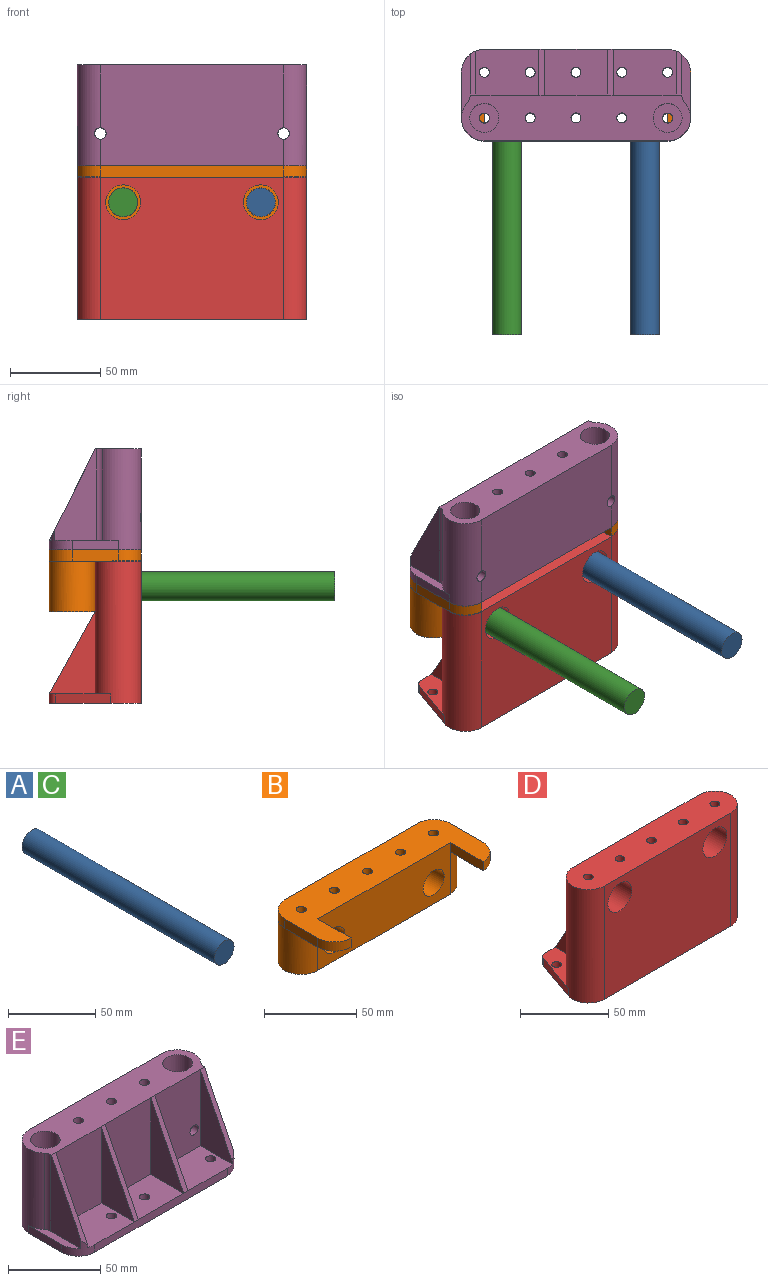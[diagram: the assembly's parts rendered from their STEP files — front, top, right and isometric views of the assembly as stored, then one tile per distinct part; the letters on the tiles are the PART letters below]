
ASSEMBLY  parts=5 mates=4
PART A: 3 faces, bbox 15.9x155.6x15.9 mm
  f0: cylinder r=7.94mm len=155.58mm, axis (0,1,0), area 7759mm2, adj f1,f2
  f1: plane 15.88x15.88mm, normal (0,-1,0), area 197.9mm2, adj f0
  f2: plane 15.88x15.88mm, normal (0,1,0), area 197.9mm2, adj f0
PART B: 29 faces, bbox 127x50.8x34.3 mm
  f0: plane 23.65x12.67mm, normal (0,0,-1), area 68.5mm2, adj f2,f7,f22
  f1: plane 25.39x6.35mm, normal (1,0,0), area 161mm2, adj f3,f5,f18,f19,f20,f21
  f2: plane 25.4x6.35mm, normal (-1,0,0), area 161.1mm2, adj f0,f8,f14,f15,f19,f22,f23
  f3: plane 24.52x12.7mm, normal (0,0,-1), area 68.9mm2, adj f1,f5,f21
  f4: plane 101.6x34.29mm, normal (0,-1,0), area 3075.2mm2, adj f5,f7,f9,f10,f12,f16,f17,f19
  f5: cylinder r=12.7mm len=34.29mm, axis (0,0,-1), area 1241.5mm2, adj f1,f3,f4,f6,f9,f19
  f6: plane 101.6x34.29mm, normal (0,1,0), area 3483.9mm2, adj f5,f7,f9,f14,f19
  f7: cylinder r=12.7mm len=27.94mm, axis (0,0,-1), area 1114.8mm2, adj f0,f4,f6,f8,f9
  f8: plane 13.58x12.7mm, normal (0,0,1), area 0.4mm2, adj f2,f7,f14
  f9: plane 127x25.4mm, normal (0,0,-1), area 2966.1mm2, adj f4,f5,f6,f7,f24,f25,f26,f27
  f10: cylinder r=8.06mm len=22.86mm, axis (0,-1,0), area 1158.3mm2, adj f4,f11
  f11: plane 16.13x16.13mm, normal (0,-1,0), area 204.3mm2, adj f10
  f12: cylinder r=8.06mm len=22.86mm, axis (0,-1,0), area 1158.3mm2, adj f4,f13
  f13: plane 16.13x16.13mm, normal (0,-1,0), area 204.3mm2, adj f12
  f14: cylinder r=12.7mm len=12.7mm, axis (0,0,-1), area 126.5mm2, adj f2,f6,f8,f19
  f15: cylinder r=12.7mm len=12.73mm, axis (0,0,-1), area 121.8mm2, adj f2,f16,f19,f23
  f16: plane 25.4x6.1mm, normal (1,0,0), area 154.8mm2, adj f4,f15,f19,f23
  f17: plane 25.4x6.1mm, normal (-1,0,0), area 154.8mm2, adj f4,f18,f19,f20
  f18: cylinder r=12.7mm len=12.73mm, axis (0,0,-1), area 121.8mm2, adj f1,f17,f19,f20
  f19: plane 126.97x50.8mm, normal (0,0,1), area 3610.5mm2, adj f1,f2,f4,f5,f6,f14,f15,f16
  f20: plane 25.4x12.73mm, normal (0,0,-1), area 253.7mm2, adj f1,f17,f18,f21
  f21: cylinder r=12.7mm len=12.67mm, axis (0,0,-1), area 4.8mm2, adj f1,f3,f4,f20
  f22: cylinder r=12.7mm len=12.67mm, axis (0,0,-1), area 4.8mm2, adj f0,f2,f4,f23
  f23: plane 25.4x12.73mm, normal (0,0,-1), area 253.7mm2, adj f2,f15,f16,f22
  f24: cylinder r=2.78mm len=34.29mm, axis (0,0,1), area 598.5mm2, adj f9,f19
  f25: cylinder r=2.78mm len=34.29mm, axis (0,0,1), area 598.5mm2, adj f9,f19
  f26: cylinder r=2.78mm len=34.29mm, axis (0,0,1), area 598.5mm2, adj f9,f19
  f27: cylinder r=2.78mm len=34.29mm, axis (0,0,1), area 598.5mm2, adj f9,f19
  f28: cylinder r=2.78mm len=34.29mm, axis (0,0,1), area 598.5mm2, adj f9,f19
PART C: same geometry as A
PART D: 40 faces, bbox 127x50.8x78.7 mm
  f0: plane 25.4x22.86mm, normal (0,0,1), area 556.4mm2, adj f5,f18,f24,f33,f35
  f1: plane 25.4x22.86mm, normal (0,0,1), area 556.4mm2, adj f5,f18,f23,f30,f32
  f2: plane 25.4x22.86mm, normal (0,0,1), area 556.4mm2, adj f5,f18,f22,f27,f29
  f3: plane 33.87x23.4mm, normal (0,0,1), area 392.5mm2, adj f5,f9,f18,f20,f21,f26,f38
  f4: plane 101.6x78.74mm, normal (0,-1,0), area 7414.6mm2, adj f6,f7,f8,f9,f10,f16
  f5: plane 101.6x73.66mm, normal (0,1,0), area 6434mm2, adj f0,f1,f2,f3,f6,f7,f8,f9
  f6: plane 127x25.4mm, normal (0,0,1), area 2966.1mm2, adj f4,f5,f9,f10,f11,f12,f13,f14
  f7: cylinder r=9.65mm len=25.4mm, axis (0,-1,0), area 1540.4mm2, adj f4,f5
  f8: cylinder r=9.65mm len=25.4mm, axis (0,-1,0), area 1540.4mm2, adj f4,f5
  f9: cylinder r=12.7mm len=78.74mm, axis (0,0,1), area 3062.2mm2, adj f3,f4,f5,f6,f16,f20
  f10: cylinder r=12.7mm len=78.74mm, axis (0,0,-1), area 3062.2mm2, adj f4,f5,f6,f16,f17,f19
  f11: cylinder r=2.78mm len=78.74mm, axis (0,0,1), area 1374.4mm2, adj f6,f16
  f12: cylinder r=2.78mm len=78.74mm, axis (0,0,1), area 1374.4mm2, adj f6,f16
  f13: cylinder r=2.78mm len=78.74mm, axis (0,0,1), area 1374.4mm2, adj f6,f16
  f14: cylinder r=2.78mm len=78.74mm, axis (0,0,1), area 1374.4mm2, adj f6,f16
  f15: cylinder r=2.78mm len=78.74mm, axis (0,0,1), area 1374.4mm2, adj f6,f16
  f16: plane 127x50.8mm, normal (0,0,-1), area 5678.4mm2, adj f4,f9,f10,f11,f12,f13,f14,f15
  f17: plane 33.87x23.4mm, normal (0,0,1), area 392.5mm2, adj f5,f10,f18,f19,f25,f36,f39
  f18: plane 94.42x5.08mm, normal (0,1,0), area 479.6mm2, adj f0,f1,f2,f3,f16,f17,f28,f31
  f19: plane 30.48x10.78mm, normal (-0.94,0.33,0), area 164.2mm2, adj f10,f16,f17,f39
  f20: plane 30.48x10.78mm, normal (0.94,0.33,0), area 164.2mm2, adj f3,f9,f16,f38
  f21: cylinder r=2.78mm len=5.56mm, axis (0,0,-1), area 88.7mm2, adj f3,f16
  f22: cylinder r=2.78mm len=5.56mm, axis (0,0,-1), area 88.7mm2, adj f2,f16
  f23: cylinder r=2.78mm len=5.56mm, axis (0,0,-1), area 88.7mm2, adj f1,f16
  f24: cylinder r=2.78mm len=5.56mm, axis (0,0,-1), area 88.7mm2, adj f0,f16
  f25: cylinder r=2.78mm len=5.56mm, axis (0,0,-1), area 88.7mm2, adj f16,f17
  f26: plane 45.72x25.4mm, normal (1,0,0), area 580.6mm2, adj f3,f5,f28
  f27: plane 45.72x25.4mm, normal (-1,0,0), area 580.6mm2, adj f2,f5,f28
  f28: plane 45.72x25.4mm, normal (0,0.87,0.49), area 132.8mm2, adj f5,f18,f26,f27
  f29: plane 45.72x25.4mm, normal (1,0,0), area 580.6mm2, adj f2,f5,f31
  f30: plane 45.72x25.4mm, normal (-1,0,0), area 580.6mm2, adj f1,f5,f31
  f31: plane 45.72x25.4mm, normal (0,0.87,0.49), area 132.8mm2, adj f5,f18,f29,f30
  f32: plane 45.72x25.4mm, normal (1,0,0), area 580.6mm2, adj f1,f5,f34
  f33: plane 45.72x25.4mm, normal (-1,0,0), area 580.6mm2, adj f0,f5,f34
  f34: plane 45.72x25.4mm, normal (0,0.87,0.49), area 132.8mm2, adj f5,f18,f32,f33
  f35: plane 45.72x25.4mm, normal (1,0,0), area 580.6mm2, adj f0,f5,f37
  f36: plane 45.72x25.4mm, normal (-1,0,0), area 580.6mm2, adj f5,f17,f37
  f37: plane 45.72x25.4mm, normal (0,0.87,0.49), area 132.8mm2, adj f5,f18,f35,f36
  f38: cylinder r=5.08mm len=5.08mm, axis (0,0,-1), area 31.8mm2, adj f3,f16,f18,f20
  f39: cylinder r=5.08mm len=5.08mm, axis (0,0,1), area 31.8mm2, adj f16,f17,f18,f19
PART E: 50 faces, bbox 127x50.8x55.9 mm
  f0: plane 101.6x55.88mm, normal (0,1,0), area 5645.7mm2, adj f1,f9,f12,f13,f16,f34
  f1: plane 127x50.8mm, normal (0,0,-1), area 6070.7mm2, adj f0,f9,f16,f18,f19,f20,f24,f25
  f2: plane 34.93x25.4mm, normal (0,0,1), area 837.2mm2, adj f3,f5,f18,f24,f28,f44,f49
  f3: plane 50.8x24.47mm, normal (-1,0,0), area 644.3mm2, adj f2,f5,f39,f49
  f4: cylinder r=3.17mm len=6.35mm, axis (0,-1,0), area 98.9mm2, adj f10,f15
  f5: plane 50.8x34.93mm, normal (0,-1,0), area 1742.5mm2, adj f2,f3,f14,f34,f44
  f6: plane 50.8x34.93mm, normal (0,-1,0), area 1774.2mm2, adj f7,f34,f41,f43
  f7: plane 34.93x25.4mm, normal (0,0,1), area 862.8mm2, adj f6,f18,f25,f41,f43
  f8: plane 35.31x4.76mm, normal (0,0,1), area 120.4mm2, adj f9,f20,f38,f46,f49
  f9: cylinder r=12.7mm len=55.88mm, axis (0,0,-1), area 1582.2mm2, adj f0,f1,f8,f13,f20,f34,f46
  f10: plane 50.8x34.93mm, normal (0,-1,0), area 1742.5mm2, adj f4,f11,f34,f36,f40
  f11: plane 34.93x25.4mm, normal (0,0,1), area 837.2mm2, adj f10,f18,f26,f27,f36,f40,f48
  f12: cylinder r=3.17mm len=6.35mm, axis (0,-1,0), area 96.9mm2, adj f0,f15,f16
  f13: cylinder r=3.17mm len=6.35mm, axis (0,-1,0), area 96.9mm2, adj f0,f9,f17
  f14: cylinder r=3.17mm len=6.35mm, axis (0,-1,0), area 98.9mm2, adj f5,f17
  f15: cylinder r=8.06mm len=50.8mm, axis (0,0,-1), area 2509.5mm2, adj f4,f12,f23,f34
  f16: cylinder r=12.7mm len=55.88mm, axis (0,0,-1), area 1582.2mm2, adj f0,f1,f12,f19,f21,f34,f47
  f17: cylinder r=8.06mm len=50.8mm, axis (0,0,-1), area 2509.5mm2, adj f13,f14,f22,f34
  f18: plane 101.6x5.08mm, normal (0,-1,0), area 516.1mm2, adj f1,f2,f7,f11,f42,f45,f48,f49
  f19: plane 25.4x5.08mm, normal (-1,0,0), area 129mm2, adj f1,f16,f21,f48
  f20: plane 25.4x5.08mm, normal (1,0,0), area 129mm2, adj f1,f8,f9,f49
  f21: plane 35.31x4.76mm, normal (0,0,1), area 120.4mm2, adj f16,f19,f35,f47,f48
  f22: plane 16.13x16.13mm, normal (0,0,1), area 180.1mm2, adj f17,f29
  f23: plane 16.13x16.13mm, normal (0,0,1), area 180.1mm2, adj f15,f33
  f24: cylinder r=2.78mm len=5.56mm, axis (0,0,1), area 88.7mm2, adj f1,f2
  f25: cylinder r=2.78mm len=5.56mm, axis (0,0,1), area 88.7mm2, adj f1,f7
  f26: cylinder r=2.78mm len=5.56mm, axis (0,0,1), area 88.7mm2, adj f1,f11
  f27: cylinder r=2.78mm len=5.56mm, axis (0,0,1), area 88.7mm2, adj f1,f11
  f28: cylinder r=2.78mm len=5.56mm, axis (0,0,1), area 88.7mm2, adj f1,f2
  f29: cylinder r=2.78mm len=5.56mm, axis (0,0,1), area 88.7mm2, adj f1,f22
  f30: cylinder r=2.78mm len=55.88mm, axis (0,0,1), area 975.4mm2, adj f1,f34
  f31: cylinder r=2.78mm len=55.88mm, axis (0,0,1), area 975.4mm2, adj f1,f34
  f32: cylinder r=2.78mm len=55.88mm, axis (0,0,1), area 975.4mm2, adj f1,f34
  f33: cylinder r=2.78mm len=5.56mm, axis (0,0,1), area 88.7mm2, adj f1,f23
  f34: plane 127x25.4mm, normal (0,0,1), area 2621.1mm2, adj f0,f5,f6,f9,f10,f15,f16,f17
  f35: plane 50.8x23.2mm, normal (-1,0,0), area 667.3mm2, adj f21,f34,f37,f47,f48
  f36: plane 50.8x24.47mm, normal (1,0,0), area 644.3mm2, adj f10,f11,f37,f48
  f37: plane 48.95x24.47mm, normal (0,-0.89,0.45), area 167.9mm2, adj f34,f35,f36,f48
  f38: plane 50.8x23.2mm, normal (1,0,0), area 667.3mm2, adj f8,f34,f39,f46,f49
  f39: plane 48.95x24.47mm, normal (0,-0.89,0.45), area 167.9mm2, adj f3,f34,f38,f49
  f40: plane 50.8x25.4mm, normal (-1,0,0), area 645.2mm2, adj f10,f11,f42
  f41: plane 50.8x25.4mm, normal (1,0,0), area 645.2mm2, adj f6,f7,f42
  f42: plane 50.8x25.4mm, normal (0,-0.89,0.45), area 180.3mm2, adj f18,f34,f40,f41
  f43: plane 50.8x25.4mm, normal (-1,0,0), area 645.2mm2, adj f6,f7,f45
  f44: plane 50.8x25.4mm, normal (1,0,0), area 645.2mm2, adj f2,f5,f45
  f45: plane 50.8x25.4mm, normal (0,-0.89,0.45), area 180.3mm2, adj f18,f34,f43,f44
  f46: cylinder r=5.08mm len=50.8mm, axis (0,0,-1), area 193.4mm2, adj f8,f9,f34,f38
  f47: cylinder r=5.08mm len=50.8mm, axis (0,0,-1), area 193.4mm2, adj f16,f21,f34,f35
  f48: cylinder r=12.7mm len=12.7mm, axis (0,0,1), area 114.5mm2, adj f1,f11,f18,f19,f21,f35,f36,f37
  f49: cylinder r=12.7mm len=12.7mm, axis (0,0,-1), area 114.5mm2, adj f1,f2,f3,f8,f18,f20,f38,f39
PLACE A t=(76.36,39.37,2.54)mm
PLACE B t=(0,39.37,2.54)mm
PLACE C rot(axis=(1,0,0),180deg) t=(0,-95.89,25.4)mm
PLACE D t=(0,39.37,2.54)mm fixed
PLACE E rot(axis=(0,0,1),180deg) t=(-0.02,13.96,39.37)mm
MATE fastened A.f0 <-> B.f10  axis (0,1,0) through (38.18,49.53,13.97)mm
MATE fastened E.f1 <-> B.f19  axis (0,0,-1) through (63.48,26.66,34.29)mm
MATE fastened C.f0 <-> B.f12  axis (0,-1,0) through (-38.18,49.53,13.97)mm
MATE slider A.f0 <-> D.f7  axis (0,1,0) through (38.18,-106.05,13.97)mm
